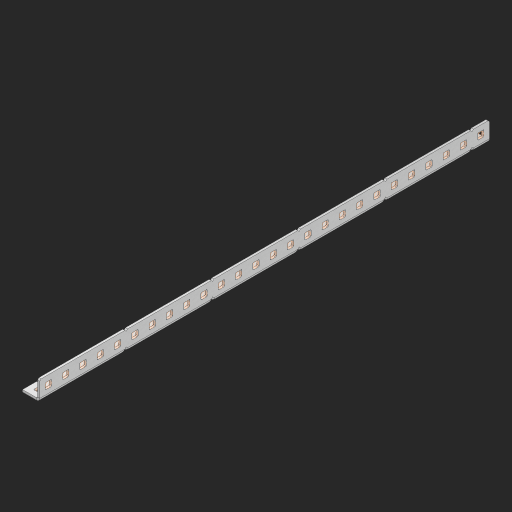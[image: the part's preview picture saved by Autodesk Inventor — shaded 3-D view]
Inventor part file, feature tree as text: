
AUTODESK INVENTOR PART (.ipt)
format: ipt  version: 2023 (Build 270158000, 158)  size: 1,152,000 bytes
history: native  units: in
note: dims shown in document units (in); Inventor stores cm internally (conversion verified against a paired STEP export)
features: other x226, extrude x76, sheet_metal_op x11, sketch x10, pattern_linear x2, mirror x1, chamfer x1
ambient origin geometry x8: Origin, YZ Plane, XZ Plane, XY Plane, X Axis, Y Axis, Z Axis, Center Point
bodies: Solid1 (feature_tree), Body (feature_tree)
feature tree (327):
  other  "Alu Half C 1x2x1x26"
  other  "Table"
  other  "Alu C 1x2x1x35"
  other  "Alu C 1x2x1x34"
  other  "Alu C 1x2x1x33"
  other  "Alu C 1x2x1x32"
  other  "Alu C 1x2x1x31"
  other  "Alu C 1x2x1x30"
  other  "Alu C 1x2x1x29"
  other  "Alu C 1x2x1x28"
  other  "Alu C 1x2x1x27"
  other  "Alu C 1x2x1x26"
  other  "Alu C 1x2x1x25"
  other  "Alu C 1x2x1x24"
  other  "Alu C 1x2x1x23"
  other  "Alu C 1x2x1x22"
  other  "Alu C 1x2x1x21"
  other  "Alu C 1x2x1x20"
  other  "Alu C 1x2x1x19"
  other  "Alu C 1x2x1x18"
  other  "Alu C 1x2x1x17"
  other  "Alu C 1x2x1x16"
  other  "Alu C 1x2x1x15"
  other  "Alu C 1x2x1x14"
  other  "Alu C 1x2x1x13"
  other  "Alu C 1x2x1x12"
  other  "Alu C 1x2x1x11"
  other  "Alu C 1x2x1x10"
  other  "Alu C 1x2x1x9"
  other  "Alu C 1x2x1x8"
  other  "Alu C 1x2x1x7"
  other  "Alu C 1x2x1x6"
  other  "Alu C 1x2x1x5"
  other  "Alu C 1x2x1x4"
  other  "Alu C 1x2x1x3"
  other  "Alu C 1x2x1x2"
  other  "Alu C 1x2x1x1"
  other  "Steel C 1x2x1x35"
  other  "Steel C 1x2x1x34"
  other  "Steel C 1x2x1x33"
  other  "Steel C 1x2x1x32"
  other  "Steel C 1x2x1x31"
  other  "Steel C 1x2x1x30"
  other  "Steel C 1x2x1x29"
  other  "Steel C 1x2x1x28"
  other  "Steel C 1x2x1x27"
  other  "Steel C 1x2x1x26"
  other  "Steel C 1x2x1x25"
  other  "Steel C 1x2x1x24"
  other  "Steel C 1x2x1x23"
  other  "Steel C 1x2x1x22"
  other  "Steel C 1x2x1x21"
  other  "Steel C 1x2x1x20"
  other  "Steel C 1x2x1x19"
  other  "Steel C 1x2x1x18"
  other  "Steel C 1x2x1x17"
  other  "Steel C 1x2x1x16"
  other  "Steel C 1x2x1x15"
  other  "Steel C 1x2x1x14"
  other  "Steel C 1x2x1x13"
  other  "Steel C 1x2x1x12"
  other  "Steel C 1x2x1x11"
  other  "Steel C 1x2x1x10"
  other  "Steel C 1x2x1x9"
  other  "Steel C 1x2x1x8"
  other  "Steel C 1x2x1x7"
  other  "Steel C 1x2x1x6"
  other  "Steel C 1x2x1x5"
  other  "Steel C 1x2x1x4"
  other  "Steel C 1x2x1x3"
  other  "Steel C 1x2x1x2"
  other  "Steel C 1x2x1x1"
  other  "Alu Half C 1x2x1x35"
  other  "Alu Half C 1x2x1x34"
  other  "Alu Half C 1x2x1x33"
  other  "Alu Half C 1x2x1x32"
  other  "Alu Half C 1x2x1x31"
  other  "Alu Half C 1x2x1x30"
  other  "Alu Half C 1x2x1x29"
  other  "Alu Half C 1x2x1x28"
  other  "Alu Half C 1x2x1x27"
  other  "Alu Half C 1x2x1x25"
  other  "Alu Half C 1x2x1x24"
  other  "Alu Half C 1x2x1x23"
  other  "Alu Half C 1x2x1x22"
  other  "Alu Half C 1x2x1x21"
  other  "Alu Half C 1x2x1x20"
  other  "Alu Half C 1x2x1x19"
  other  "Alu Half C 1x2x1x18"
  other  "Alu Half C 1x2x1x17"
  other  "Alu Half C 1x2x1x16"
  other  "Alu Half C 1x2x1x15"
  other  "Alu Half C 1x2x1x14"
  other  "Alu Half C 1x2x1x13"
  other  "Alu Half C 1x2x1x12"
  other  "Alu Half C 1x2x1x11"
  other  "Alu Half C 1x2x1x10"
  other  "Alu Half C 1x2x1x9"
  other  "Alu Half C 1x2x1x8"
  other  "Alu Half C 1x2x1x7"
  other  "Alu Half C 1x2x1x6"
  other  "Alu Half C 1x2x1x5"
  other  "Alu Half C 1x2x1x4"
  other  "Alu Half C 1x2x1x3"
  other  "Alu Half C 1x2x1x2"
  other  "Alu Half C 1x2x1x1"
  other  "Steel Half C 1x2x1x35"
  other  "Steel Half C 1x2x1x34"
  other  "Steel Half C 1x2x1x33"
  other  "Steel Half C 1x2x1x32"
  other  "Steel Half C 1x2x1x31"
  other  "Steel Half C 1x2x1x30"
  other  "Steel Half C 1x2x1x29"
  other  "Steel Half C 1x2x1x28"
  other  "Steel Half C 1x2x1x27"
  other  "Steel Half C 1x2x1x26"
  other  "Steel Half C 1x2x1x25"
  other  "Steel Half C 1x2x1x24"
  other  "Steel Half C 1x2x1x23"
  other  "Steel Half C 1x2x1x22"
  other  "Steel Half C 1x2x1x21"
  other  "Steel Half C 1x2x1x20"
  other  "Steel Half C 1x2x1x19"
  other  "Steel Half C 1x2x1x18"
  other  "Steel Half C 1x2x1x17"
  other  "Steel Half C 1x2x1x16"
  other  "Steel Half C 1x2x1x15"
  other  "Steel Half C 1x2x1x14"
  other  "Steel Half C 1x2x1x13"
  other  "Steel Half C 1x2x1x12"
  other  "Steel Half C 1x2x1x11"
  other  "Steel Half C 1x2x1x10"
  other  "Steel Half C 1x2x1x9"
  other  "Steel Half C 1x2x1x8"
  other  "Steel Half C 1x2x1x7"
  other  "Steel Half C 1x2x1x6"
  other  "Steel Half C 1x2x1x5"
  other  "Steel Half C 1x2x1x4"
  other  "Steel Half C 1x2x1x3"
  other  "Steel Half C 1x2x1x2"
  other  "Steel Half C 1x2x1x1"
  sheet_metal_op  "Flanges"
  other  "Flange Pattern Plane"
  other  "Flange Pattern Sketch"
  sheet_metal_op  "Flange Pattern"
  sheet_metal_op  "Body Pattern"
  pattern_linear  "Center Pattern"  Spacing1=0.0625in  [1 undecoded]
  other  "Arc Length"
  mirror  "Notch Mirror"
  pattern_linear  "Notch Pattern"  Spacing1=0.182in  [1 undecoded]
  chamfer  "End Chamfer"
  extrude  "Half Cut"  Depth=0.02in
  sketch  "Sketch1"  dims[d0=1.0in]
  other  "Plate1"
  sketch  "Sketch2"  dims[d1=13.0in]
  other  "Plate2"
  sheet_metal_op  "Bend1"
  sheet_metal_op  "Corner1"
  sketch  "Sketch3"  dims[d2=0.0625in]
  sketch  "Sketch7"  dims[d3=0.0625in]
  other  "Srf1"
  other  "Srf2"
  sketch  "Sketch8"  dims[d4=0.0312in]
  sketch  "Sketch9"  dims[d5=0.125in]
  other  "Srf91"
  sheet_metal_op  "Body Pattern Sketch"
  other  "Srf92"
  sketch  "Sketch13"  dims[d6=0.0625in]
  sketch  "Sketch14"  dims[d7=0.5in d8=90.0deg d9=0.0312in]
  sketch  "Sketch15"  dims[d10=0.25in]
  sketch  "Sketch16"  dims[d11=0.0625in d12=0.0625in d16=0.182in d17=0.02in d18=0.0625in d19=0.0in d20=0.25in d21=0.25in d38=10.2362in d40=0.5in d41=0.3937in d43=1.0in d46=0.172in d47=1.0in d48=0.0in d49=0.182in d50=0.02in d51=0.25in d52=0.25in d53=0.0625in d54=0.0in d55=0.172in d56=1.0in d57=0.0in d58=0.25in d60=10.2362in d62=0.5in d63=0.3937in d65=0.5in d85=0.1473in d86=0.1782in d88=0.04in d89=0.0625in d90=0.0in d91=0.04in d92=0.0491in d95=2.5in d96=0.04in d97=0.25in d98=45.0deg d99=0.25in d100=0.5in d101=0.0in d102=2.497in d106=0.182in d107=0.02in d108=0.5in d109=0.5in d110=0.0625in d111=0.0in d112=0.172in d113=0.5in d114=0.0in d117=0.5in d118=0.5in d119=0.5in]
  other  "Srf786"
  other  "Srf823"
  other  "Srf824"
  other  "Srf825"
  other  "Srf826"
  other  "Srf827"
  other  "Srf828"
  other  "Srf829"
  other  "Srf856"
  other  "Srf857"
  other  "Srf858"
  other  "Srf859"
  other  "Srf860"
  other  "Srf861"
  other  "Srf862"
  other  "Srf889"
  other  "Srf890"
  other  "Srf891"
  other  "Srf892"
  other  "Srf893"
  other  "Srf894"
  other  "Srf895"
  other  "Srf896"
  other  "Srf922"
  other  "Srf923"
  other  "Srf924"
  other  "Srf925"
  other  "Srf926"
  other  "Srf959"
  other  "Srf960"
  other  "Srf961"
  other  "Srf962"
  other  "Srf963"
  other  "Srf996"
  other  "Srf997"
  other  "Srf998"
  other  "Srf999"
  other  "Srf1000"
  other  "Srf1143"
  other  "Srf1144"
  other  "Srf1145"
  other  "Srf1146"
  other  "Srf1147"
  other  "Srf1148"
  other  "Srf1149"
  other  "Srf1150"
  other  "Srf1151"
  other  "Srf1152"
  other  "Srf1153"
  other  "Srf1154"
  other  "Srf1199"
  other  "Srf1200"
  other  "Srf1201"
  other  "Srf1202"
  other  "Srf1203"
  other  "Srf1204"
  other  "Srf1205"
  other  "Srf1206"
  other  "Srf1207"
  other  "Srf1208"
  other  "Srf1209"
  other  "Srf1210"
  other  "Srf1255"
  other  "Srf1256"
  other  "Srf1257"
  other  "Srf1258"
  other  "Srf1259"
  other  "Srf1260"
  other  "Srf1261"
  other  "Srf1262"
  other  "Srf1263"
  other  "Srf1264"
  other  "Srf1265"
  other  "Srf1266"
  sheet_metal_op  "Flange Stamp"
  sheet_metal_op  "Flange Circle"
  sheet_metal_op  "Body Stamp"
  sheet_metal_op  "Body Circle"
  other  "Center Stamp"
  other  "Center Circle"
  sheet_metal_op  "Notch"
  extrude  "ExtrusionSrf2"  Depth=0.0625in
  extrude  "ExtrusionSrf92"  TaperAngle=0.0deg  [1 undecoded]
  extrude  "ExtrusionSrf823"  Depth=0.25in
  extrude  "ExtrusionSrf824"  Depth=0.25in
  extrude  "ExtrusionSrf825"  Depth=0.5in
  extrude  "ExtrusionSrf826"  Depth=0.5in
  extrude  "ExtrusionSrf827"  Depth=1.0in TaperAngle=0.0deg
  extrude  "ExtrusionSrf828"  Depth=0.182in
  extrude  "ExtrusionSrf829"  Depth=0.02in
  extrude  "ExtrusionSrf856"  Depth=0.25in
  extrude  "ExtrusionSrf857"  Depth=0.25in
  extrude  "ExtrusionSrf858"  Depth=0.0625in
  extrude  "ExtrusionSrf859"  TaperAngle=0.0deg  [1 undecoded]
  extrude  "ExtrusionSrf860"  Depth=0.5in
  extrude  "ExtrusionSrf861"  Depth=1.0in TaperAngle=0.0deg
  extrude  "ExtrusionSrf862"  Depth=0.25in
  extrude  "ExtrusionSrf889"  Depth=0.5in
  extrude  "ExtrusionSrf890"  Depth=0.5in
  extrude  "ExtrusionSrf891"  Depth=0.5in
  extrude  "ExtrusionSrf892"  Depth=0.5in
  extrude  "ExtrusionSrf893"  Depth=0.5in
  extrude  "ExtrusionSrf894"  Depth=0.0625in
  extrude  "ExtrusionSrf895"  TaperAngle=0.0deg  [1 undecoded]
  extrude  "ExtrusionSrf896"  Depth=0.5in
  extrude  "ExtrusionSrf922"  Depth=0.5in
  extrude  "ExtrusionSrf923"  Depth=2.5in
  extrude  "ExtrusionSrf924"  Depth=0.25in TaperAngle=45.0deg
  extrude  "ExtrusionSrf925"  Depth=0.25in
  extrude  "ExtrusionSrf926"  Depth=0.5in TaperAngle=0.0deg
  extrude  "ExtrusionSrf959"  Depth=0.5in
  extrude  "ExtrusionSrf960"  Depth=0.182in
  extrude  "ExtrusionSrf961"  Depth=0.02in
  extrude  "ExtrusionSrf962"  Depth=0.5in
  extrude  "ExtrusionSrf963"  Depth=0.5in
  extrude  "ExtrusionSrf996"  Depth=0.0625in
  extrude  "ExtrusionSrf997"  TaperAngle=0.0deg  [1 undecoded]
  extrude  "ExtrusionSrf998"  Depth=0.5in
  extrude  "ExtrusionSrf999"  Depth=0.5in TaperAngle=0.0deg
  extrude  "ExtrusionSrf1000"  Depth=0.5in
  extrude  "ExtrusionSrf1143"  Depth=0.5in
  extrude  "ExtrusionSrf1144"  Depth=0.5in
  extrude  "ExtrusionSrf1145"  [1 undecoded]
  extrude  "ExtrusionSrf1146"  [1 undecoded]
  extrude  "ExtrusionSrf1147"  [1 undecoded]
  extrude  "ExtrusionSrf1148"  [1 undecoded]
  extrude  "ExtrusionSrf1149"  [1 undecoded]
  extrude  "ExtrusionSrf1150"  [1 undecoded]
  extrude  "ExtrusionSrf1151"  [1 undecoded]
  extrude  "ExtrusionSrf1152"  [1 undecoded]
  extrude  "ExtrusionSrf1153"  [1 undecoded]
  extrude  "ExtrusionSrf1154"  [1 undecoded]
  extrude  "ExtrusionSrf1199"  [1 undecoded]
  extrude  "ExtrusionSrf1200"  [1 undecoded]
  extrude  "ExtrusionSrf1201"  [1 undecoded]
  extrude  "ExtrusionSrf1202"  [1 undecoded]
  extrude  "ExtrusionSrf1203"  [1 undecoded]
  extrude  "ExtrusionSrf1204"  [1 undecoded]
  extrude  "ExtrusionSrf1205"  [1 undecoded]
  extrude  "ExtrusionSrf1206"  [1 undecoded]
  extrude  "ExtrusionSrf1207"  [1 undecoded]
  extrude  "ExtrusionSrf1208"  [1 undecoded]
  extrude  "ExtrusionSrf1209"  [1 undecoded]
  extrude  "ExtrusionSrf1210"  [1 undecoded]
  extrude  "ExtrusionSrf1255"  [1 undecoded]
  extrude  "ExtrusionSrf1256"  [1 undecoded]
  extrude  "ExtrusionSrf1257"  [1 undecoded]
  extrude  "ExtrusionSrf1258"  [1 undecoded]
  extrude  "ExtrusionSrf1259"  [1 undecoded]
  extrude  "ExtrusionSrf1260"  [1 undecoded]
  extrude  "ExtrusionSrf1261"  [1 undecoded]
  extrude  "ExtrusionSrf1262"  [1 undecoded]
  extrude  "ExtrusionSrf1263"  [1 undecoded]
  extrude  "ExtrusionSrf1264"  [1 undecoded]
  extrude  "ExtrusionSrf1265"  [1 undecoded]
  extrude  "ExtrusionSrf1266"  [1 undecoded]
note: 40 required parameter values undecoded (feature->parameter linkage not recoverable at this tier; creation-order binding heuristic only, values carry confidence <= 0.55)
